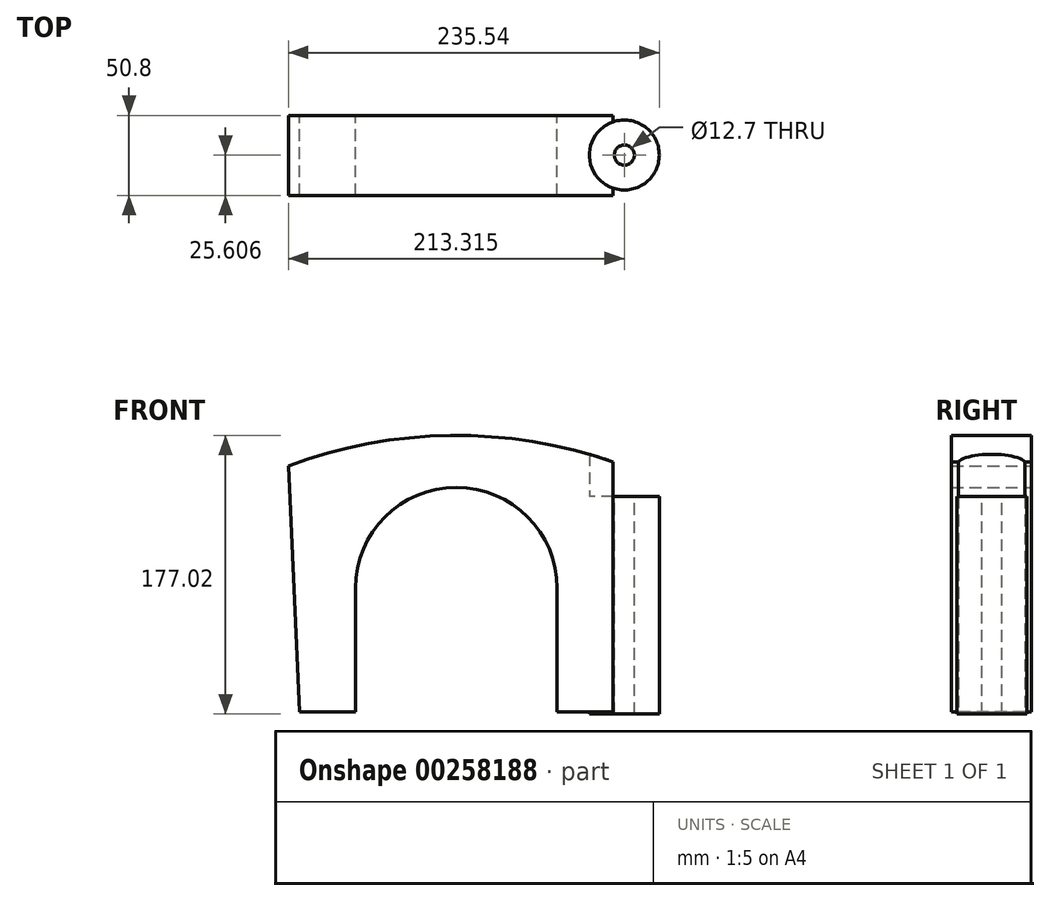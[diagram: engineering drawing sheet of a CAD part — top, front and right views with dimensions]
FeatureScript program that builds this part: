
annotation { "Feature Type Name" : "Feature", "Feature Type Description" : "" }
export const myFeature = defineFeature(function(context is Context, id is Id, definition is map)
    precondition{}
    {
        {
            var Q0;
            Q0=qCreatedBy(makeId("Front.planeOp"),FACE);
            var sketch = newSketch(context, id + "F0", { "sketchPlane" : qUnion([Q0])});
            skArc(sketch, "E0", {"start": v(64.05, 0) * mm, "mid": v(0, 64.05) * mm, "end": v(-64.05, 0) * mm});
            skLineSegment(sketch, "E1", {"start": v(64.05, 0) * mm, "end": v(64.05, -78.5) * mm});
            skLineSegment(sketch, "E2", {"start": v(-64.05, 0) * mm, "end": v(-64.05, -78.5) * mm});
            skLineSegment(sketch, "E3", {"start": v(-106.64, 77.68) * mm, "end": v(106.64, 77.68) * mm});
            skArc(sketch, "E4", {"start": v(106.64, 77.68) * mm, "mid": v(0, 97) * mm, "end": v(-106.64, 77.68) * mm});
            skLineSegment(sketch, "E5", {"start": v(-64.05, -78.5) * mm, "end": v(-99.6, -78.5) * mm});
            skLineSegment(sketch, "E6", {"start": v(64.05, -78.5) * mm, "end": v(99.6, -78.5) * mm});
            skLineSegment(sketch, "E7", {"start": v(-106.64, 77.68) * mm, "end": v(-99.6, -78.5) * mm});
            skLineSegment(sketch, "E8", {"start": v(106.64, 77.68) * mm, "end": v(99.6, -78.5) * mm});
            skSolve(sketch);
        }
        {
            var Q0;
            Q0=makeQuery(id+"F0.imprint","IMPRINT",FACE,{"disambiguationData":[TD([[makeQuery(id+"F0.imprint","IMPRINT",EDGE,{"derivedFrom":sQuery(id+"F0.wireOp",EDGE,"E0")}),-1.0]])]});
            var Q1;
            Q1=makeQuery(id+"F0.imprint","IMPRINT",FACE,{"disambiguationData":[TD([[makeQuery(id+"F0.imprint","IMPRINT",EDGE,{"derivedFrom":sQuery(id+"F0.wireOp",EDGE,"E3")}),1.0]])]});
            extrude(context, id + "F1", {"entities" : qUnion([Q0, Q1]), "depth" : 50.8 * mm});
        }
        {
            var Q0;
            Q0=qCreatedBy(makeId("Top.planeOp"),FACE);
            var sketch = newSketch(context, id + "F2", { "sketchPlane" : qUnion([Q0])});
            skCircle(sketch, "E9", {"center": v(106.68, -25.2) * mm, "radius": 22.23 * mm});
            skSolve(sketch);
        }
        {
            var Q0;
            Q0=makeQuery(id+"F2.imprint","IMPRINT",FACE,{"disambiguationData":[TD([[makeQuery(id+"F2.imprint","IMPRINT",EDGE,{"derivedFrom":sQuery(id+"F2.wireOp",EDGE,"E9")}),1.0]])]});
            extrude(context, id + "F3", {"entities" : qUnion([Q0]), "operationType" : NewBodyOperationType.ADD, "oppositeDirection" : true, "depth" : 80 * mm});
        }
        {
            var Q0;
            Q0=makeQuery(id+"F2.imprint","IMPRINT",FACE,{"disambiguationData":[TD([[makeQuery(id+"F2.imprint","IMPRINT",EDGE,{"derivedFrom":sQuery(id+"F2.wireOp",EDGE,"E9")}),1.0]])]});
            extrude(context, id + "F4", {"entities" : qUnion([Q0]), "operationType" : NewBodyOperationType.ADD, "depth" : 58.17 * mm});
        }
        {
            var Q0;
            Q0=makeQuery(id+"F4.opExtrude","CAP_FACE",FACE,{"disambiguationData":[OSD([sQuery(id+"F2.wireOp",EDGE,"E9")])],"isStart":false});
            var sketch = newSketch(context, id + "F5", { "sketchPlane" : qUnion([Q0])});
            skCircle(sketch, "E10", {"center": v(106.68, -25.2) * mm, "radius": 22.23 * mm});
            skSolve(sketch);
        }
        {
            var Q0;
            Q0=makeQuery(id+"F5.imprint","IMPRINT",FACE,{"disambiguationData":[TD([[makeQuery(id+"F5.imprint","IMPRINT",EDGE,{"derivedFrom":sQuery(id+"F5.wireOp",EDGE,"E10")}),1.0]])]});
            var Q1;
            {var subQ0=sQuery(id+"F0.wireOp",EDGE,"E6");var subQ1=sQuery(id+"F0.wireOp",EDGE,"E4");var subQ2=sQuery(id+"F2.wireOp",EDGE,"E9");var subQ3=sQuery(id+"F0.wireOp",EDGE,"E8");var subQ4=sQuery(id+"F0.wireOp",EDGE,"E7");var subQ5=sQuery(id+"F0.wireOp",EDGE,"E5");var subQ6=sQuery(id+"F0.wireOp",EDGE,"E2");var subQ7=sQuery(id+"F0.wireOp",EDGE,"E1");var subQ8=sQuery(id+"F0.wireOp",EDGE,"E0");Q1=makeQuery(id+"F4.boolean.opBoolean","SPLIT",FACE,{"disambiguationData":[TD([makeQuery(id+"F1.opExtrude","CAP_FACE",FACE,{"disambiguationData":[OSD([subQ8,subQ7,subQ6,subQ1,subQ5,subQ0,subQ4,subQ3])],"isStart":true}),makeQuery(id+"F1.opExtrude","CAP_FACE",FACE,{"disambiguationData":[OSD([subQ8,subQ7,subQ6,subQ1,subQ5,subQ0,subQ4,subQ3])],"isStart":false}),makeQuery(id+"F1.opExtrude","SWEPT_FACE",FACE,{"disambiguationData":[OSD([subQ1])]}),makeQuery(id+"F1.opExtrude","SWEPT_FACE",FACE,{"disambiguationData":[OSD([subQ0])]}),makeQuery(id+"F3.opExtrude","SWEPT_FACE",FACE,{"disambiguationData":[OSD([subQ2])]}),makeQuery(id+"F4.opExtrude","SWEPT_FACE",FACE,{"disambiguationData":[OSD([subQ2])]}),makeQuery(id+"F4.opExtrude","CAP_FACE",FACE,{"disambiguationData":[OSD([subQ2])],"isStart":false})])],"derivedFrom":makeQuery(id+"F1.opExtrude","SWEPT_FACE",FACE,{"disambiguationData":[OSD([subQ3])]})});}
            extrude(context, id + "F6", {"entities" : qUnion([Q0, Q1]), "operationType" : NewBodyOperationType.REMOVE, "endBound" : BoundingType.THROUGH_ALL, "depth" : 3.8 * mm});
        }
        {
            var Q0;
            Q0=sQuery(id+"F5.wireOp",VERTEX,"E10.center");
            var Q1;
            Q1=makeQuery(id+"F1.opExtrude","SWEPT_BODY",BODY,{"disambiguationData":[OSD([sQuery(id+"F0.wireOp",EDGE,"E0"),sQuery(id+"F0.wireOp",EDGE,"E1"),sQuery(id+"F0.wireOp",EDGE,"E2"),sQuery(id+"F0.wireOp",EDGE,"E4"),sQuery(id+"F0.wireOp",EDGE,"E5"),sQuery(id+"F0.wireOp",EDGE,"E6"),sQuery(id+"F0.wireOp",EDGE,"E7"),sQuery(id+"F0.wireOp",EDGE,"E8")])]});
            hole(context, id + "F7", {"style" : HoleStyle.SIMPLE, "endStyle" : HoleEndStyle.THROUGH, "holeDiameter" : 12.7 * mm, "tappedDepth" : 12.7 * mm, "tapClearance" : 3, "locations" : qUnion([Q0]), "scope" : qUnion([Q1])});
        }
    });
